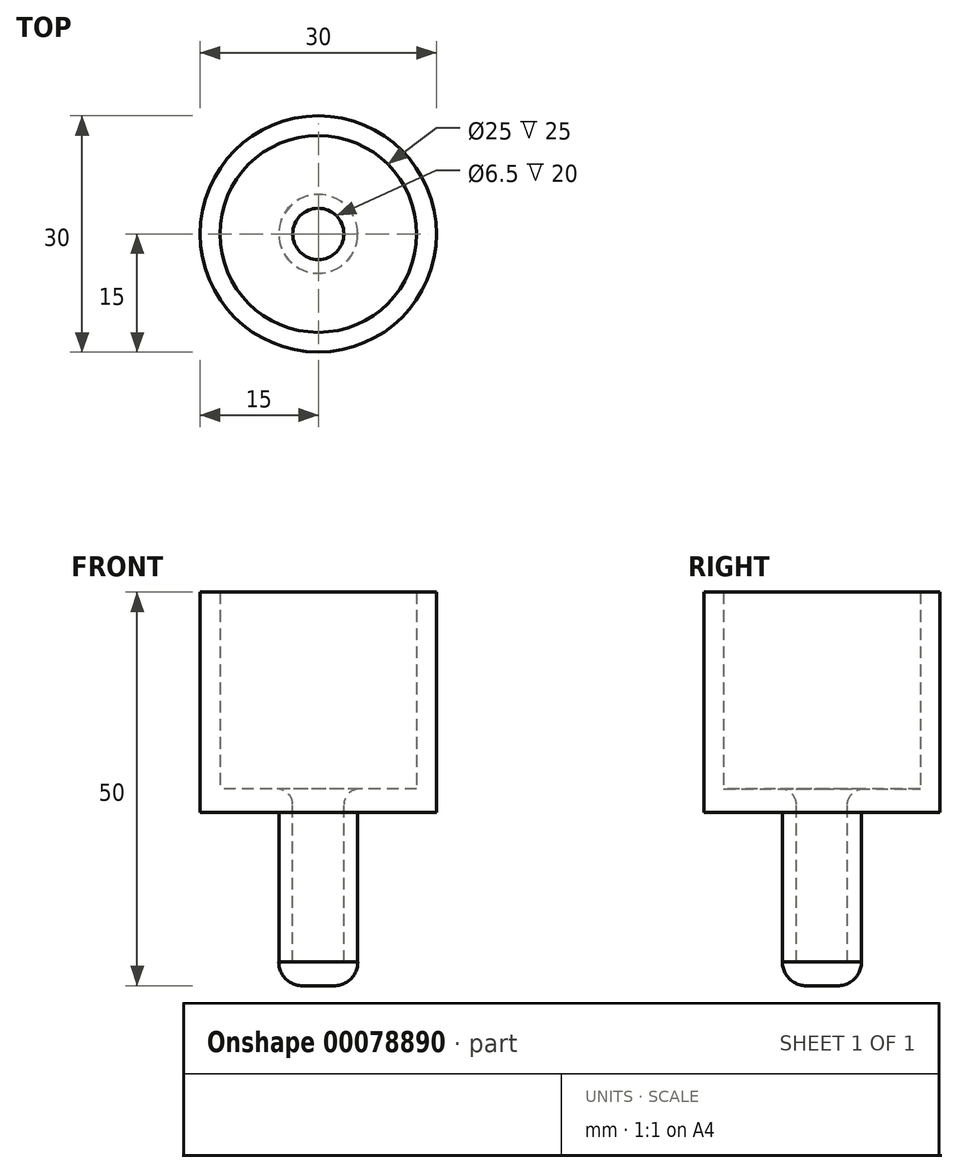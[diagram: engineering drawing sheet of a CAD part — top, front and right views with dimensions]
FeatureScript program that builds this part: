
annotation { "Feature Type Name" : "Feature", "Feature Type Description" : "" }
export const myFeature = defineFeature(function(context is Context, id is Id, definition is map)
    precondition{}
    {
        {
            var Q0;
            Q0=qCreatedBy(makeId("Top.planeOp"),FACE);
            var sketch = newSketch(context, id + "F0", { "sketchPlane" : qUnion([Q0])});
            skPoint(sketch, "E0", {"position": v(0, 0) * mm});
            skCircle(sketch, "E1", {"center": v(0, 0) * mm, "radius": 15 * mm});
            skCircle(sketch, "E2", {"center": v(0, 0) * mm, "radius": 12.5 * mm});
            skCircle(sketch, "E3", {"center": v(0, 0) * mm, "radius": 3.25 * mm});
            skCircle(sketch, "E4", {"center": v(0, 0) * mm, "radius": 5 * mm});
            skSolve(sketch);
        }
        {
            var Q0;
            Q0 = qSketchRegion(id + "F0", true);
            extrude(context, id + "F7", {"entities" : qUnion([Q0]), "depth" : 25 * mm});
        }
        {
            var Q0;
            Q0 = qSketchRegion(id + "F0", true);
            var Q1;
            Q1=makeQuery(id+"F0.imprint","IMPRINT",FACE,{"disambiguationData":[TD([[makeQuery(id+"F0.imprint","IMPRINT",EDGE,{"derivedFrom":sQuery(id+"F0.wireOp",EDGE,"E2")}),1.0]])]});
            extrude(context, id + "F1", {"entities" : qUnion([Q0, Q1]), "operationType" : NewBodyOperationType.ADD, "oppositeDirection" : true, "depth" : 3 * mm});
        }
        {
            var Q0;
            Q0=makeQuery(id+"F0.imprint","IMPRINT",FACE,{"disambiguationData":[TD([[makeQuery(id+"F0.imprint","IMPRINT",EDGE,{"derivedFrom":sQuery(id+"F0.wireOp",EDGE,"E3")}),-1.0]])]});
            extrude(context, id + "F2", {"entities" : qUnion([Q0]), "operationType" : NewBodyOperationType.ADD, "oppositeDirection" : true, "depth" : 22 * mm});
        }
        {
            var Q0;
            Q0=makeQuery(id+"F2.opExtrude","CAP_FACE",FACE,{"disambiguationData":[OSD([sQuery(id+"F0.wireOp",EDGE,"E3"),sQuery(id+"F0.wireOp",EDGE,"E4")])],"isStart":false});
            var sketch = newSketch(context, id + "F3", { "sketchPlane" : qUnion([Q0])});
            skCircle(sketch, "E5", {"center": v(0, 0) * mm, "radius": 5.02 * mm});
            skSolve(sketch);
        }
        {
            var Q0;
            Q0 = qSketchRegion(id + "F3", true);
            extrude(context, id + "F4", {"entities" : qUnion([Q0]), "operationType" : NewBodyOperationType.ADD, "depth" : 3 * mm});
        }
        {
            var Q0;
            Q0=makeQuery(id+"F4.opExtrude","CAP_EDGE",EDGE,{"disambiguationData":[OSD([sQuery(id+"F3.wireOp",EDGE,"E5")])],"isStart":false});
            fillet(context, id + "F5", {"entities" : qUnion([Q0]), "radius" : 3 * mm, "tangentPropagation" : true, "allowEdgeOverflow" : false});
        }
        {
            var Q0;
            Q0=makeQuery(id+"F2.opExtrude","CAP_EDGE",EDGE,{"disambiguationData":[OSD([sQuery(id+"F0.wireOp",EDGE,"E3")])],"isStart":true});
            fillet(context, id + "F6", {"entities" : qUnion([Q0]), "radius" : 2 * mm, "tangentPropagation" : true, "allowEdgeOverflow" : false});
        }
    });
